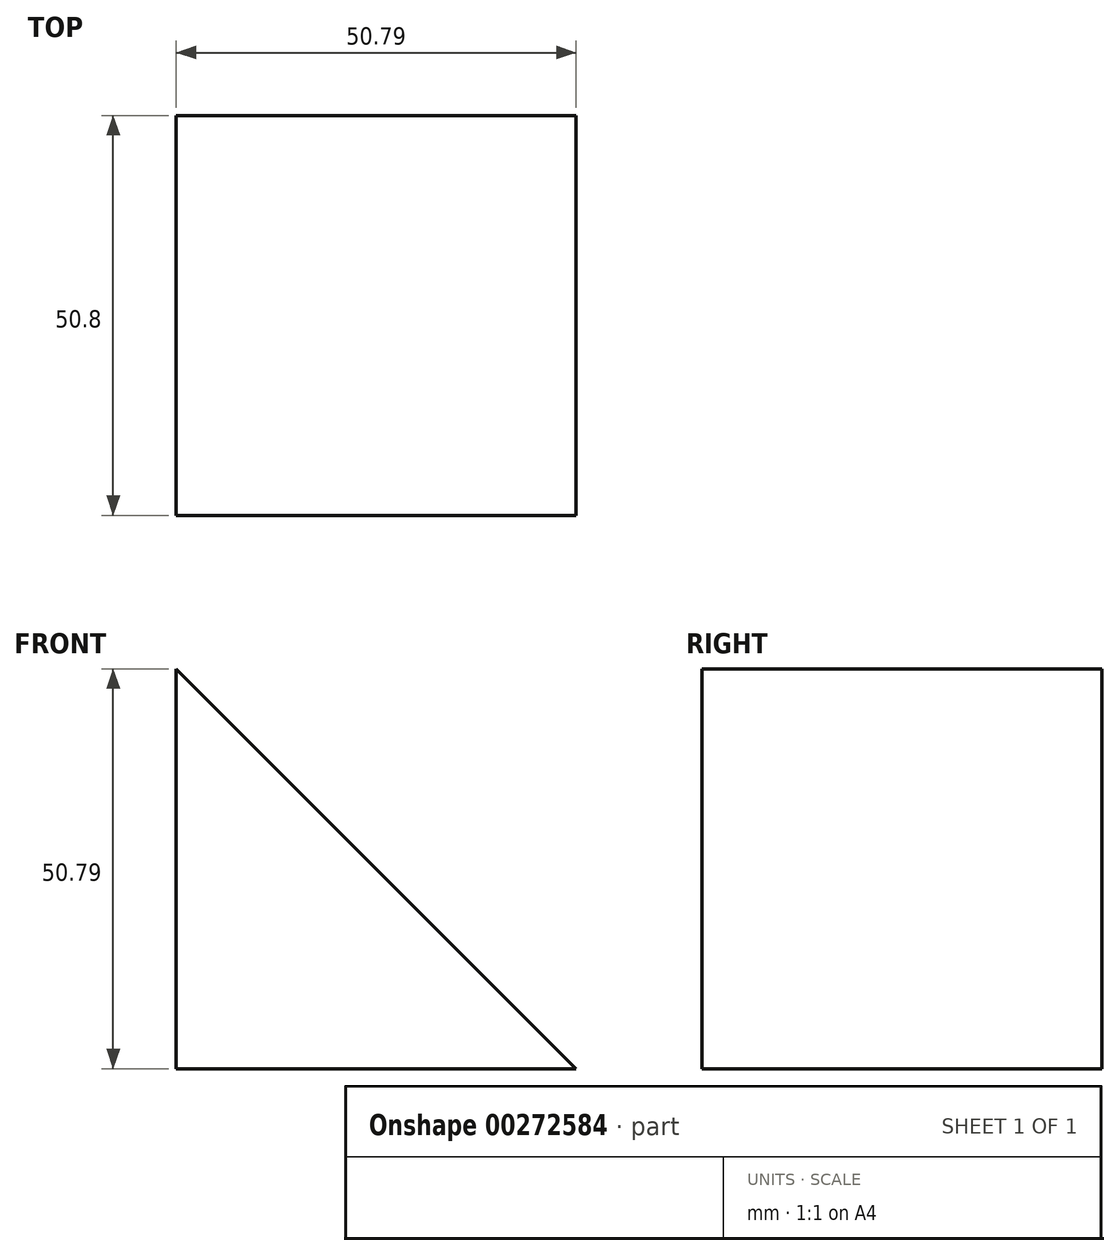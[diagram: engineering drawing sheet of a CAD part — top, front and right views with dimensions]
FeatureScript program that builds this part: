
annotation { "Feature Type Name" : "Feature", "Feature Type Description" : "" }
export const myFeature = defineFeature(function(context is Context, id is Id, definition is map)
    precondition{}
    {
        {
            var Q0;
            Q0=qCreatedBy(makeId("Front.planeOp"),FACE);
            var sketch = newSketch(context, id + "F0", { "sketchPlane" : qUnion([Q0])});
            skLineSegment(sketch, "E0", {"start": v(-56.71, 50.8) * mm, "end": v(-56.71, 0) * mm});
            skLineSegment(sketch, "E1", {"start": v(-56.71, 0) * mm, "end": v(-5.92, 0) * mm});
            skLineSegment(sketch, "E2", {"start": v(-5.92, 0) * mm, "end": v(-56.71, 50.8) * mm});
            skSolve(sketch);
        }
        {
            var Q0;
            Q0 = qSketchRegion(id + "F0", true);
            extrude(context, id + "F1", {"entities" : qUnion([Q0]), "depth" : 50.8 * mm});
        }
    });
